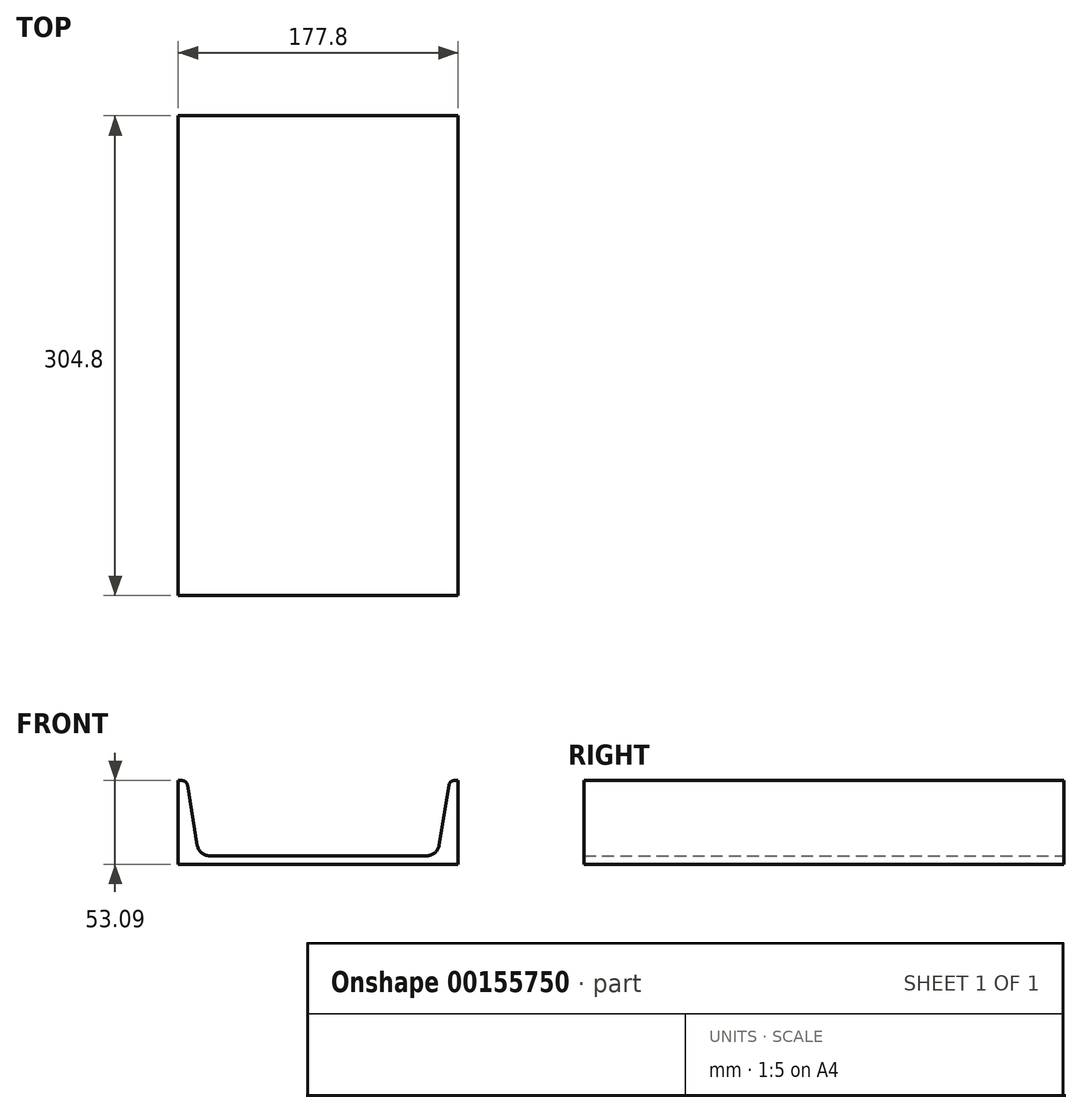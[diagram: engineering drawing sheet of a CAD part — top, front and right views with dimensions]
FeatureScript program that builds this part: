
annotation { "Feature Type Name" : "Feature", "Feature Type Description" : "" }
export const myFeature = defineFeature(function(context is Context, id is Id, definition is map)
    precondition{}
    {
        {
            var Q0;
            Q0=qCreatedBy(makeId("Front.planeOp"),FACE);
            var sketch = newSketch(context, id + "F0", { "sketchPlane" : qUnion([Q0])});
            skLineSegment(sketch, "E0", {"start": v(0, 138.03) * mm, "end": v(0, 0) * mm, "construction": true});
            skLineSegment(sketch, "E1", {"start": v(0, 0) * mm, "end": v(88.9, 0) * mm});
            skLineSegment(sketch, "E2", {"start": v(88.9, 0) * mm, "end": v(88.9, 53.09) * mm});
            skLineSegment(sketch, "E3", {"start": v(88.9, 53.09) * mm, "end": v(83.57, 53.09) * mm});
            skLineSegment(sketch, "E4", {"start": v(83.57, 53.09) * mm, "end": v(75.7, 5.33) * mm});
            skLineSegment(sketch, "E5", {"start": v(75.7, 5.33) * mm, "end": v(0, 5.33) * mm});
            skLineSegment(sketch, "E6.MirrorCS", {"start": v(-88.9, 0) * mm, "end": v(-88.9, 53.09) * mm});
            skLineSegment(sketch, "E7.MirrorCS", {"start": v(-75.7, 5.33) * mm, "end": v(0, 5.33) * mm});
            skLineSegment(sketch, "E8.MirrorCS", {"start": v(-83.57, 53.09) * mm, "end": v(-75.7, 5.33) * mm});
            skLineSegment(sketch, "E9.MirrorCS", {"start": v(0, 0) * mm, "end": v(-88.9, 0) * mm});
            skLineSegment(sketch, "E10.MirrorCS", {"start": v(-88.9, 53.09) * mm, "end": v(-83.57, 53.09) * mm});
            skSolve(sketch);
        }
        {
            var Q0;
            Q0 = qSketchRegion(id + "F0", true);
            extrude(context, id + "F1", {"entities" : qUnion([Q0]), "depth" : 304.8 * mm, "symmetric" : true});
        }
        {
            var Q0;
            Q0=makeQuery(id+"F1.opExtrude","SWEPT_EDGE",EDGE,{"disambiguationData":[OSD([sQuery(id+"F0.wireOp",EDGE,"E7.MirrorCS"),sQuery(id+"F0.wireOp",EDGE,"E8.MirrorCS")])]});
            var Q1;
            Q1=makeQuery(id+"F1.opExtrude","SWEPT_EDGE",EDGE,{"disambiguationData":[OSD([sQuery(id+"F0.wireOp",EDGE,"E4"),sQuery(id+"F0.wireOp",EDGE,"E5")])]});
            fillet(context, id + "F2", {"entities" : qUnion([Q0, Q1]), "radius" : 7.87 * mm, "tangentPropagation" : true, "allowEdgeOverflow" : false});
        }
        {
            var Q0;
            Q0=makeQuery(id+"F1.opExtrude","SWEPT_EDGE",EDGE,{"disambiguationData":[OSD([sQuery(id+"F0.wireOp",EDGE,"E3"),sQuery(id+"F0.wireOp",EDGE,"E4")])]});
            var Q1;
            Q1=makeQuery(id+"F1.opExtrude","SWEPT_EDGE",EDGE,{"disambiguationData":[OSD([sQuery(id+"F0.wireOp",EDGE,"E8.MirrorCS"),sQuery(id+"F0.wireOp",EDGE,"E10.MirrorCS")])]});
            fillet(context, id + "F3", {"entities" : qUnion([Q0, Q1]), "radius" : 3.3 * mm, "tangentPropagation" : true, "allowEdgeOverflow" : false});
        }
    });
